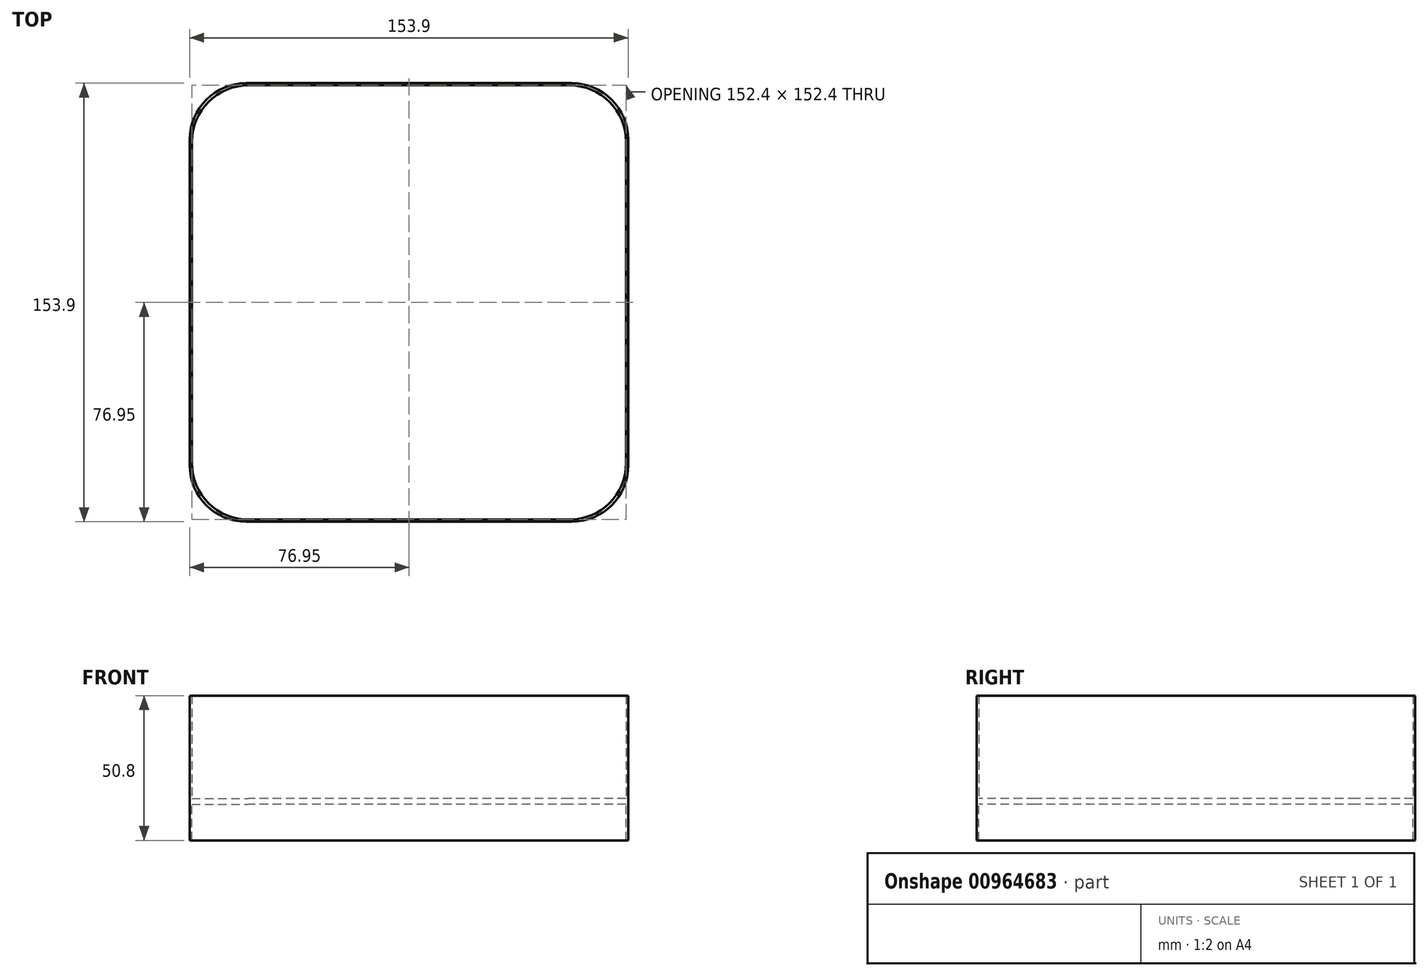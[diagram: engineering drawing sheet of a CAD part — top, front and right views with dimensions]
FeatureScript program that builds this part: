
annotation { "Feature Type Name" : "Feature", "Feature Type Description" : "" }
export const myFeature = defineFeature(function(context is Context, id is Id, definition is map)
    precondition{}
    {
        {
            var Q0;
            Q0=qCreatedBy(makeId("Top.planeOp"),FACE);
            var sketch = newSketch(context, id + "F0", { "sketchPlane" : qUnion([Q0])});
            skLineSegment(sketch, "E0.bottom", {"start": v(56.39, 76.2) * mm, "end": v(-56.39, 76.2) * mm});
            skLineSegment(sketch, "E0.top", {"start": v(56.39, -76.2) * mm, "end": v(-56.39, -76.2) * mm});
            skLineSegment(sketch, "E0.left", {"start": v(76.2, 56.39) * mm, "end": v(76.2, -56.39) * mm});
            skLineSegment(sketch, "E0.right", {"start": v(-76.2, 56.39) * mm, "end": v(-76.2, -56.39) * mm});
            skPoint(sketch, "E0.middle", {"position": v(0, 0) * mm});
            skPoint(sketch, "E1.visualSharp", {"position": v(76.2, 76.2) * mm});
            skArc(sketch, "E1.filletArc", {"start": v(76.2, 56.39) * mm, "mid": v(70.4, 70.4) * mm, "end": v(56.39, 76.2) * mm});
            skPoint(sketch, "E2.visualSharp", {"position": v(-76.2, 76.2) * mm});
            skArc(sketch, "E2.filletArc", {"start": v(-56.39, 76.2) * mm, "mid": v(-70.4, 70.4) * mm, "end": v(-76.2, 56.39) * mm});
            skPoint(sketch, "E3.visualSharp", {"position": v(-76.2, -76.2) * mm});
            skArc(sketch, "E3.filletArc", {"start": v(-76.2, -56.39) * mm, "mid": v(-70.4, -70.4) * mm, "end": v(-56.39, -76.2) * mm});
            skPoint(sketch, "E4.visualSharp", {"position": v(76.2, -76.2) * mm});
            skArc(sketch, "E4.filletArc", {"start": v(56.39, -76.2) * mm, "mid": v(70.4, -70.4) * mm, "end": v(76.2, -56.39) * mm});
            skLineSegment(sketch, "E5.bottom", {"start": v(57.14, 76.95) * mm, "end": v(-57.14, 76.95) * mm});
            skLineSegment(sketch, "E5.top", {"start": v(57.14, -76.95) * mm, "end": v(-57.14, -76.95) * mm});
            skLineSegment(sketch, "E5.left", {"start": v(76.95, 57.14) * mm, "end": v(76.95, -57.14) * mm});
            skLineSegment(sketch, "E5.right", {"start": v(-76.95, 57.14) * mm, "end": v(-76.95, -57.14) * mm});
            skLineSegment(sketch, "E6.bottom", {"start": v(-18.13, -79.76) * mm, "end": v(-18.13, -79.76) * mm});
            skLineSegment(sketch, "E6.top", {"start": v(-18.13, -74.14) * mm, "end": v(-18.13, -74.14) * mm});
            skLineSegment(sketch, "E6.left", {"start": v(-18.13, -79.76) * mm, "end": v(-18.13, -74.14) * mm});
            skLineSegment(sketch, "E6.right", {"start": v(-18.13, -79.76) * mm, "end": v(-18.13, -74.14) * mm});
            skPoint(sketch, "E6.middle", {"position": v(-18.13, -76.95) * mm});
            skPoint(sketch, "E7.visualSharp", {"position": v(-76.95, -76.95) * mm});
            skArc(sketch, "E7.filletArc", {"start": v(-76.95, -57.14) * mm, "mid": v(-71.15, -71.15) * mm, "end": v(-57.14, -76.95) * mm});
            skPoint(sketch, "E8.visualSharp", {"position": v(76.95, -76.95) * mm});
            skArc(sketch, "E8.filletArc", {"start": v(57.14, -76.95) * mm, "mid": v(71.15, -71.15) * mm, "end": v(76.95, -57.14) * mm});
            skPoint(sketch, "E9.visualSharp", {"position": v(-76.95, 76.95) * mm});
            skArc(sketch, "E9.filletArc", {"start": v(-57.14, 76.95) * mm, "mid": v(-71.15, 71.15) * mm, "end": v(-76.95, 57.14) * mm});
            skPoint(sketch, "E10.visualSharp", {"position": v(76.95, 76.95) * mm});
            skArc(sketch, "E10.filletArc", {"start": v(76.95, 57.14) * mm, "mid": v(71.15, 71.15) * mm, "end": v(57.14, 76.95) * mm});
            skSolve(sketch);
        }
        {
            var Q0;
            Q0=makeQuery(id+"F0.imprint","IMPRINT",FACE,{"disambiguationData":[TD([[makeQuery(id+"F0.imprint","IMPRINT",EDGE,{"derivedFrom":sQuery(id+"F0.wireOp",EDGE,"E0.bottom")}),-1.0]])]});
            extrude(context, id + "F1", {"entities" : qUnion([Q0]), "depth" : 38.1 * mm, "offsetDistance" : 25.4 * mm});
        }
        {
            var Q0;
            Q0=makeQuery(id+"F0.imprint","IMPRINT",FACE,{"disambiguationData":[TD([[makeQuery(id+"F0.imprint","IMPRINT",EDGE,{"derivedFrom":sQuery(id+"F0.wireOp",EDGE,"E0.bottom")}),1.0]])]});
            extrude(context, id + "F2", {"entities" : qUnion([Q0]), "operationType" : NewBodyOperationType.ADD, "depth" : 2 * mm, "offsetDistance" : 25.4 * mm});
        }
        {
            var Q0;
            Q0=makeQuery(id+"F0.imprint","IMPRINT",FACE,{"disambiguationData":[TD([[makeQuery(id+"F0.imprint","IMPRINT",EDGE,{"derivedFrom":sQuery(id+"F0.wireOp",EDGE,"E0.bottom")}),-1.0]])]});
            extrude(context, id + "F3", {"entities" : qUnion([Q0]), "operationType" : NewBodyOperationType.ADD, "oppositeDirection" : true, "depth" : 12.7 * mm, "offsetDistance" : 25.4 * mm});
        }
    });
